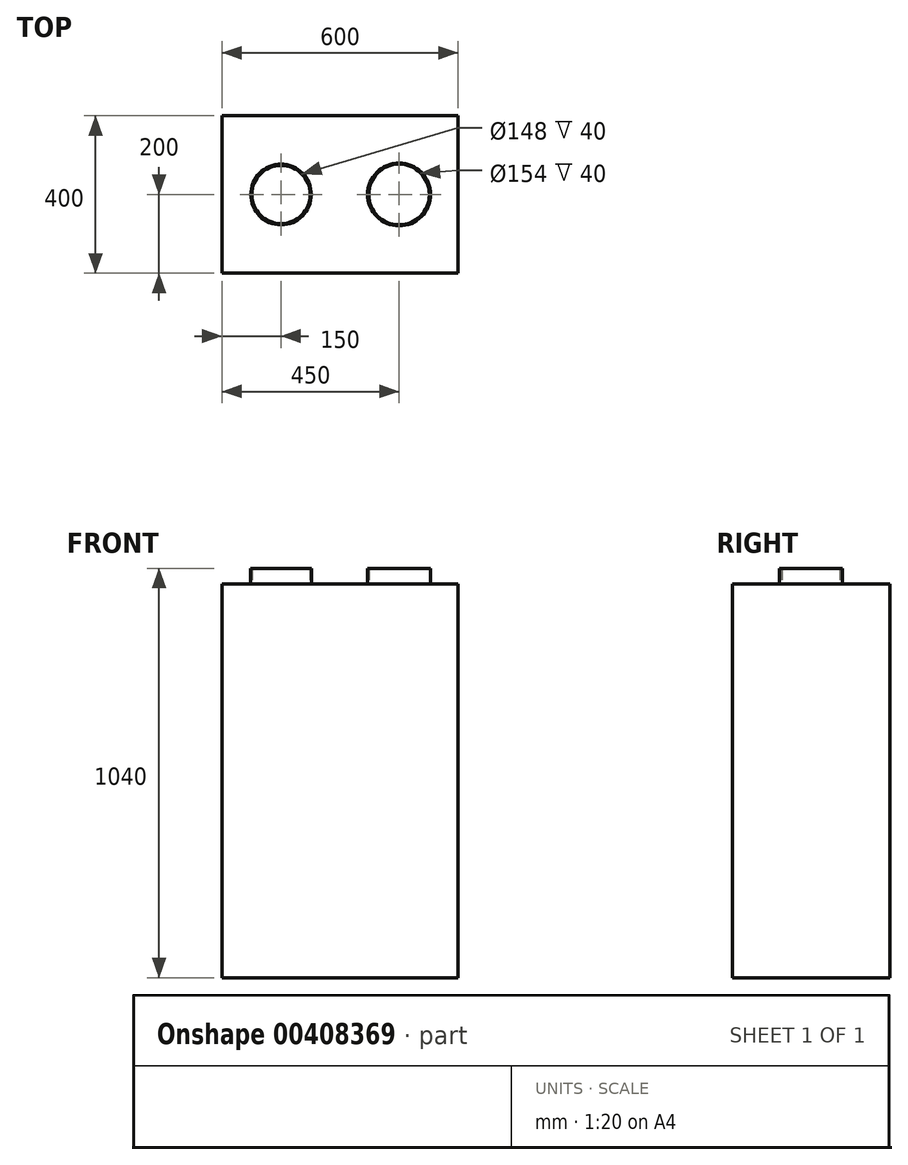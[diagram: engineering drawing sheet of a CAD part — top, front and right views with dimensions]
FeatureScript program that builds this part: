
annotation { "Feature Type Name" : "Feature", "Feature Type Description" : "" }
export const myFeature = defineFeature(function(context is Context, id is Id, definition is map)
    precondition{}
    {
        {
            var Q0;
            Q0=qCreatedBy(makeId("Top.planeOp"),FACE);
            var sketch = newSketch(context, id + "F0", { "sketchPlane" : qUnion([Q0])});
            skLineSegment(sketch, "E0.bottom", {"start": v(-600, 0) * mm, "end": v(0, 0) * mm});
            skLineSegment(sketch, "E0.top", {"start": v(-600, -400) * mm, "end": v(0, -400) * mm});
            skLineSegment(sketch, "E0.left", {"start": v(-600, 0) * mm, "end": v(-600, -400) * mm});
            skLineSegment(sketch, "E0.right", {"start": v(0, 0) * mm, "end": v(0, -400) * mm});
            skSolve(sketch);
        }
        {
            var Q0;
            Q0=makeQuery(id+"F0.imprint","IMPRINT",FACE,{"disambiguationData":[TD([[makeQuery(id+"F0.imprint","IMPRINT",EDGE,{"derivedFrom":sQuery(id+"F0.wireOp",EDGE,"E0.bottom")}),-1.0]])]});
            extrude(context, id + "F1", {"entities" : qUnion([Q0]), "depth" : 1000 * mm});
        }
        {
            var Q0;
            Q0=makeQuery(id+"F1.opExtrude","CAP_FACE",FACE,{"disambiguationData":[OSD([sQuery(id+"F0.wireOp",EDGE,"E0.bottom"),sQuery(id+"F0.wireOp",EDGE,"E0.top"),sQuery(id+"F0.wireOp",EDGE,"E0.left"),sQuery(id+"F0.wireOp",EDGE,"E0.right")])],"isStart":false});
            var sketch = newSketch(context, id + "F2", { "sketchPlane" : qUnion([Q0])});
            skCircle(sketch, "E1", {"center": v(-450, -200) * mm, "radius": 77 * mm});
            skCircle(sketch, "E2", {"center": v(-150, -200) * mm, "radius": 77 * mm});
            skLineSegment(sketch, "E3", {"start": v(-600, -200) * mm, "end": v(0, -200) * mm, "construction": true});
            skLineSegment(sketch, "E4", {"start": v(-300, 0) * mm, "end": v(-300, -200) * mm, "construction": true});
            skCircle(sketch, "E5", {"center": v(-150, -200) * mm, "radius": 80 * mm});
            skCircle(sketch, "E6", {"center": v(-450, -200) * mm, "radius": 74 * mm});
            skSolve(sketch);
        }
        {
            var Q0;
            Q0 = qSketchRegion(id + "F2", true);
            extrude(context, id + "F3", {"entities" : qUnion([Q0]), "operationType" : NewBodyOperationType.ADD, "depth" : 40 * mm});
        }
    });
